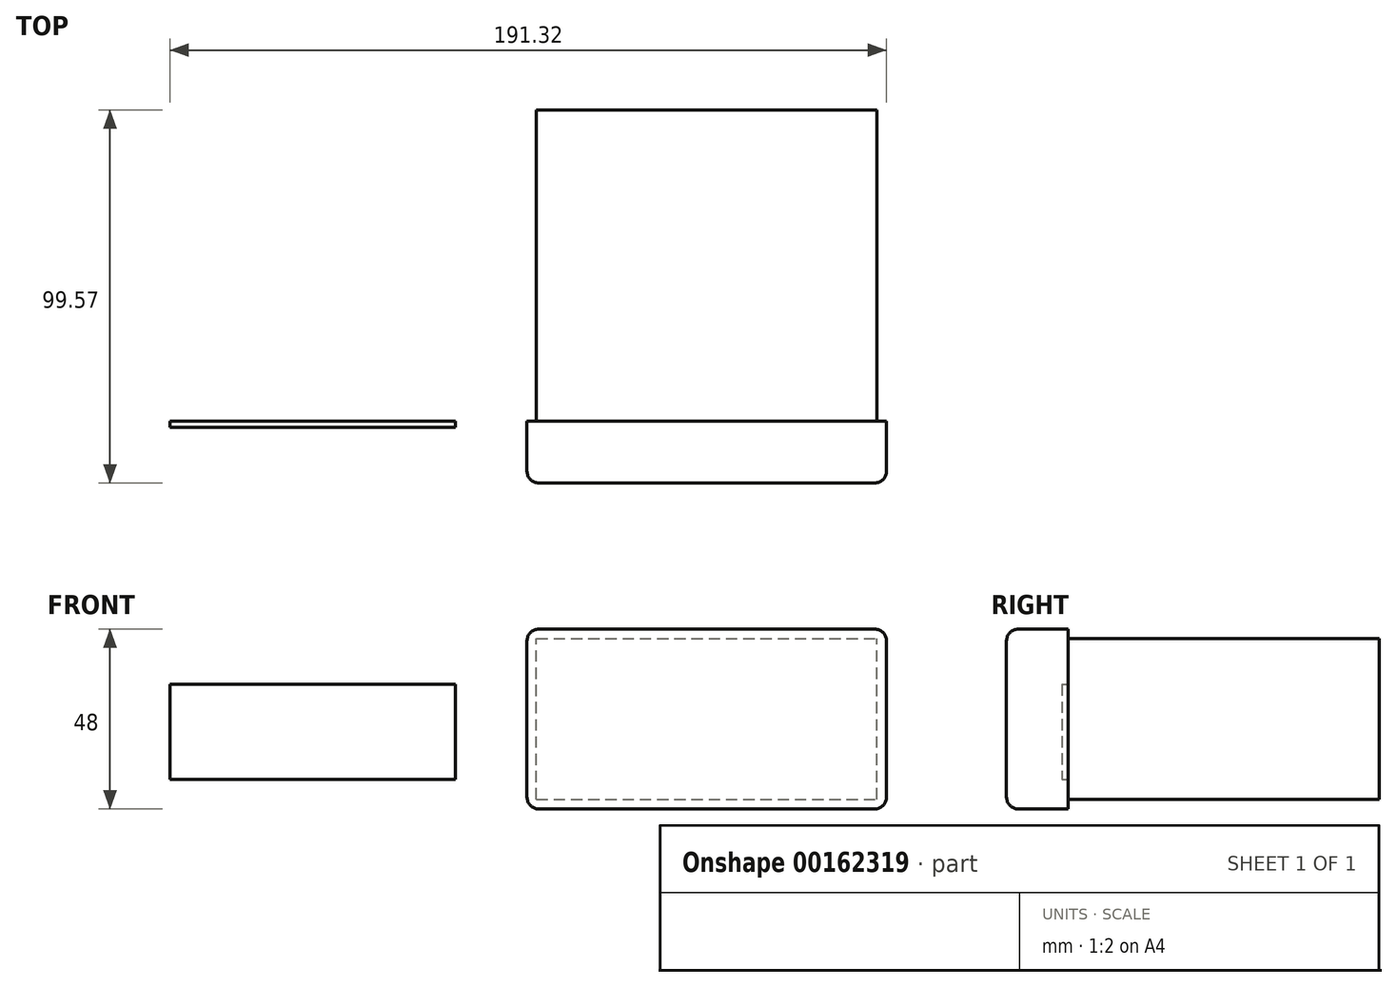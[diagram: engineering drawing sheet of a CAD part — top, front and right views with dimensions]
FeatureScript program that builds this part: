
annotation { "Feature Type Name" : "Feature", "Feature Type Description" : "" }
export const myFeature = defineFeature(function(context is Context, id is Id, definition is map)
    precondition{}
    {
        {
            var Q0;
            Q0=qCreatedBy(makeId("Front.planeOp"),FACE);
            var sketch = newSketch(context, id + "F0", { "sketchPlane" : qUnion([Q0])});
            skLineSegment(sketch, "E0.bottom", {"start": v(-44.83, 24) * mm, "end": v(44.83, 24) * mm});
            skLineSegment(sketch, "E0.top", {"start": v(-44.83, -24) * mm, "end": v(44.83, -24) * mm});
            skLineSegment(sketch, "E0.left", {"start": v(-48, 20.83) * mm, "end": v(-48, -20.83) * mm});
            skLineSegment(sketch, "E0.right", {"start": v(48, 20.83) * mm, "end": v(48, -20.83) * mm});
            skPoint(sketch, "E0.middle", {"position": v(0, 0) * mm});
            skPoint(sketch, "E1.visualSharp", {"position": v(-48, 24) * mm});
            skArc(sketch, "E1.filletArc", {"start": v(-44.83, 24) * mm, "mid": v(-47.08, 23.07) * mm, "end": v(-48, 20.83) * mm});
            skPoint(sketch, "E2.visualSharp", {"position": v(48, 24) * mm});
            skArc(sketch, "E2.filletArc", {"start": v(48, 20.83) * mm, "mid": v(47.08, 23.07) * mm, "end": v(44.83, 24) * mm});
            skPoint(sketch, "E3.visualSharp", {"position": v(48, -24) * mm});
            skArc(sketch, "E3.filletArc", {"start": v(44.83, -24) * mm, "mid": v(47.08, -23.07) * mm, "end": v(48, -20.83) * mm});
            skPoint(sketch, "E4.visualSharp", {"position": v(-48, -24) * mm});
            skArc(sketch, "E4.filletArc", {"start": v(-48, -20.83) * mm, "mid": v(-47.08, -23.07) * mm, "end": v(-44.83, -24) * mm});
            skSolve(sketch);
        }
        {
            var Q0;
            Q0 = qSketchRegion(id + "F0", true);
            extrude(context, id + "F1", {"entities" : qUnion([Q0]), "depth" : 16.5 * mm});
        }
        {
            var Q0;
            Q0=makeQuery(id+"F1.opExtrude","CAP_FACE",FACE,{"disambiguationData":[OSD([sQuery(id+"F0.wireOp",EDGE,"E0.bottom"),sQuery(id+"F0.wireOp",EDGE,"E0.top"),sQuery(id+"F0.wireOp",EDGE,"E0.left"),sQuery(id+"F0.wireOp",EDGE,"E0.right"),sQuery(id+"F0.wireOp",EDGE,"E1.filletArc"),sQuery(id+"F0.wireOp",EDGE,"E2.filletArc"),sQuery(id+"F0.wireOp",EDGE,"E3.filletArc"),sQuery(id+"F0.wireOp",EDGE,"E4.filletArc")])],"isStart":true});
            var sketch = newSketch(context, id + "F2", { "sketchPlane" : qUnion([Q0])});
            skLineSegment(sketch, "E5.bottom", {"start": v(45.47, -21.46) * mm, "end": v(-45.47, -21.46) * mm});
            skLineSegment(sketch, "E5.top", {"start": v(45.47, 21.46) * mm, "end": v(-45.47, 21.46) * mm});
            skLineSegment(sketch, "E5.left", {"start": v(45.47, -21.46) * mm, "end": v(45.47, 21.46) * mm});
            skLineSegment(sketch, "E5.right", {"start": v(-45.47, -21.46) * mm, "end": v(-45.47, 21.46) * mm});
            skPoint(sketch, "E5.middle", {"position": v(0, 0) * mm});
            skSolve(sketch);
        }
        {
            var Q0;
            Q0=makeQuery(id+"F2.imprint","IMPRINT",FACE,{"disambiguationData":[TD([[makeQuery(id+"F2.imprint","IMPRINT",EDGE,{"derivedFrom":sQuery(id+"F2.wireOp",EDGE,"E5.bottom")}),-1.0]])]});
            extrude(context, id + "F3", {"entities" : qUnion([Q0]), "operationType" : NewBodyOperationType.ADD, "depth" : 83.06 * mm});
        }
        {
            var Q0;
            Q0=qCreatedBy(makeId("Front.planeOp"),FACE);
            var sketch = newSketch(context, id + "F4", { "sketchPlane" : qUnion([Q0])});
            skLineSegment(sketch, "E6.bottom", {"start": v(-67.11, 9.22) * mm, "end": v(-143.31, 9.22) * mm});
            skLineSegment(sketch, "E6.top", {"start": v(-67.11, -16.18) * mm, "end": v(-143.31, -16.18) * mm});
            skLineSegment(sketch, "E6.left", {"start": v(-67.11, 9.22) * mm, "end": v(-67.11, -16.18) * mm});
            skLineSegment(sketch, "E6.right", {"start": v(-143.31, 9.22) * mm, "end": v(-143.31, -16.18) * mm});
            skSolve(sketch);
        }
        {
            var Q0;
            Q0=makeQuery(id+"F4.imprint","IMPRINT",FACE,{"disambiguationData":[TD([[makeQuery(id+"F4.imprint","IMPRINT",EDGE,{"derivedFrom":sQuery(id+"F4.wireOp",EDGE,"E6.bottom")}),1.0]])]});
            extrude(context, id + "F5", {"entities" : qUnion([Q0]), "depth" : 1.65 * mm});
        }
        {
            var Q0;
            Q0=makeQuery(id+"F1.opExtrude","CAP_EDGE",EDGE,{"disambiguationData":[OSD([sQuery(id+"F0.wireOp",EDGE,"E0.top")])],"isStart":false});
            fillet(context, id + "F6", {"entities" : qUnion([Q0]), "radius" : 3.17 * mm, "tangentPropagation" : true, "allowEdgeOverflow" : false});
        }
    });
